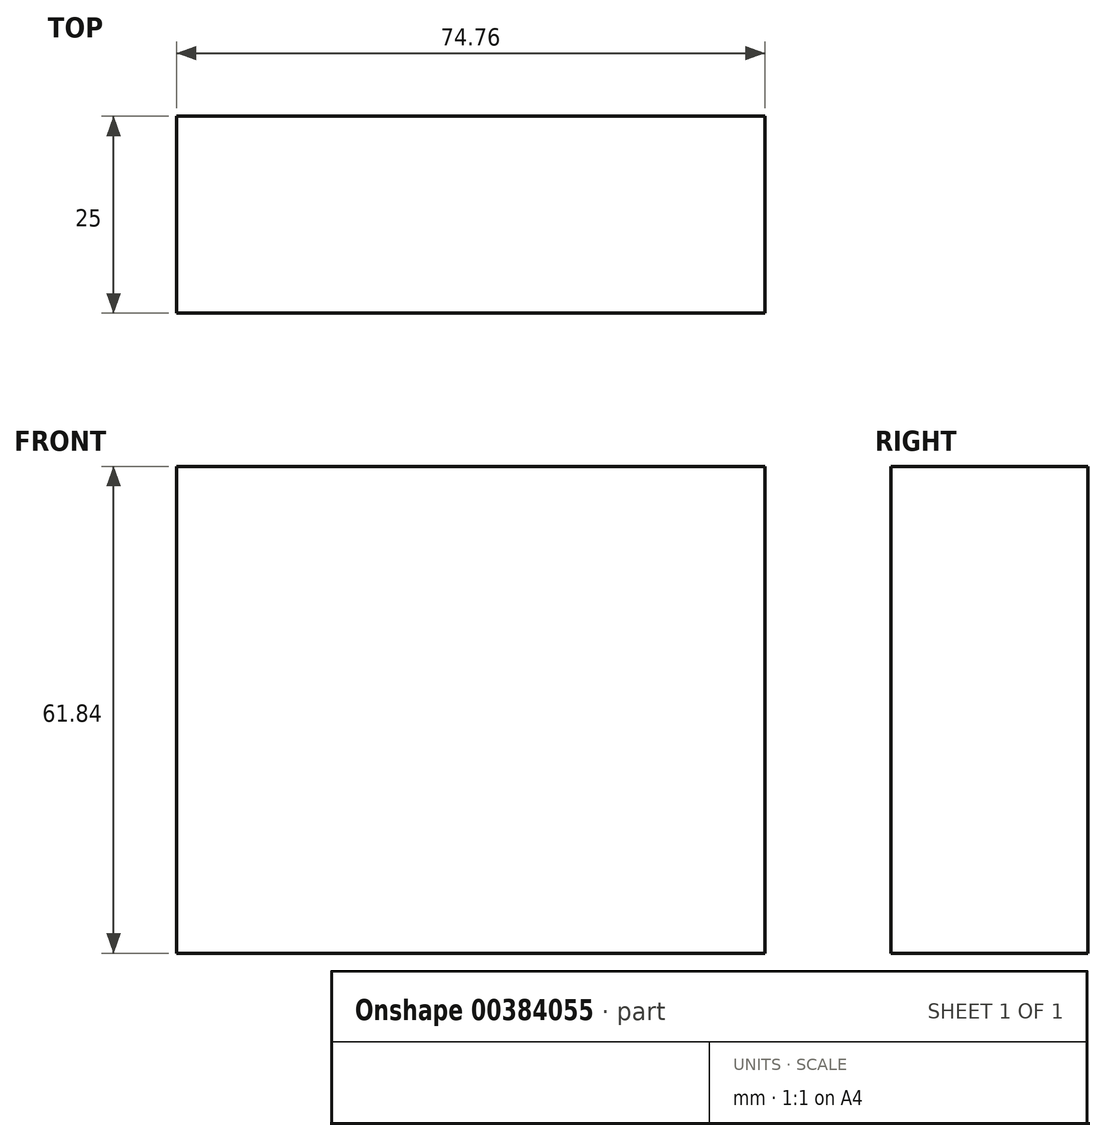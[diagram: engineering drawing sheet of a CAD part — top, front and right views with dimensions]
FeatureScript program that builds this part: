
annotation { "Feature Type Name" : "Feature", "Feature Type Description" : "" }
export const myFeature = defineFeature(function(context is Context, id is Id, definition is map)
    precondition{}
    {
        {
            var Q0;
            Q0=qCreatedBy(makeId("Front.planeOp"),FACE);
            var sketch = newSketch(context, id + "F0", { "sketchPlane" : qUnion([Q0])});
            skLineSegment(sketch, "E0.bottom", {"start": v(37.38, -30.92) * mm, "end": v(-37.38, -30.92) * mm});
            skLineSegment(sketch, "E0.top", {"start": v(37.38, 30.92) * mm, "end": v(-37.38, 30.92) * mm});
            skLineSegment(sketch, "E0.left", {"start": v(37.38, -30.92) * mm, "end": v(37.38, 30.92) * mm});
            skLineSegment(sketch, "E0.right", {"start": v(-37.38, -30.92) * mm, "end": v(-37.38, 30.92) * mm});
            skPoint(sketch, "E0.middle", {"position": v(0, 0) * mm});
            skSolve(sketch);
        }
        {
            var Q0;
            Q0 = qSketchRegion(id + "F0", true);
            extrude(context, id + "F1", {"entities" : qUnion([Q0]), "depth" : 25 * mm});
        }
    });
